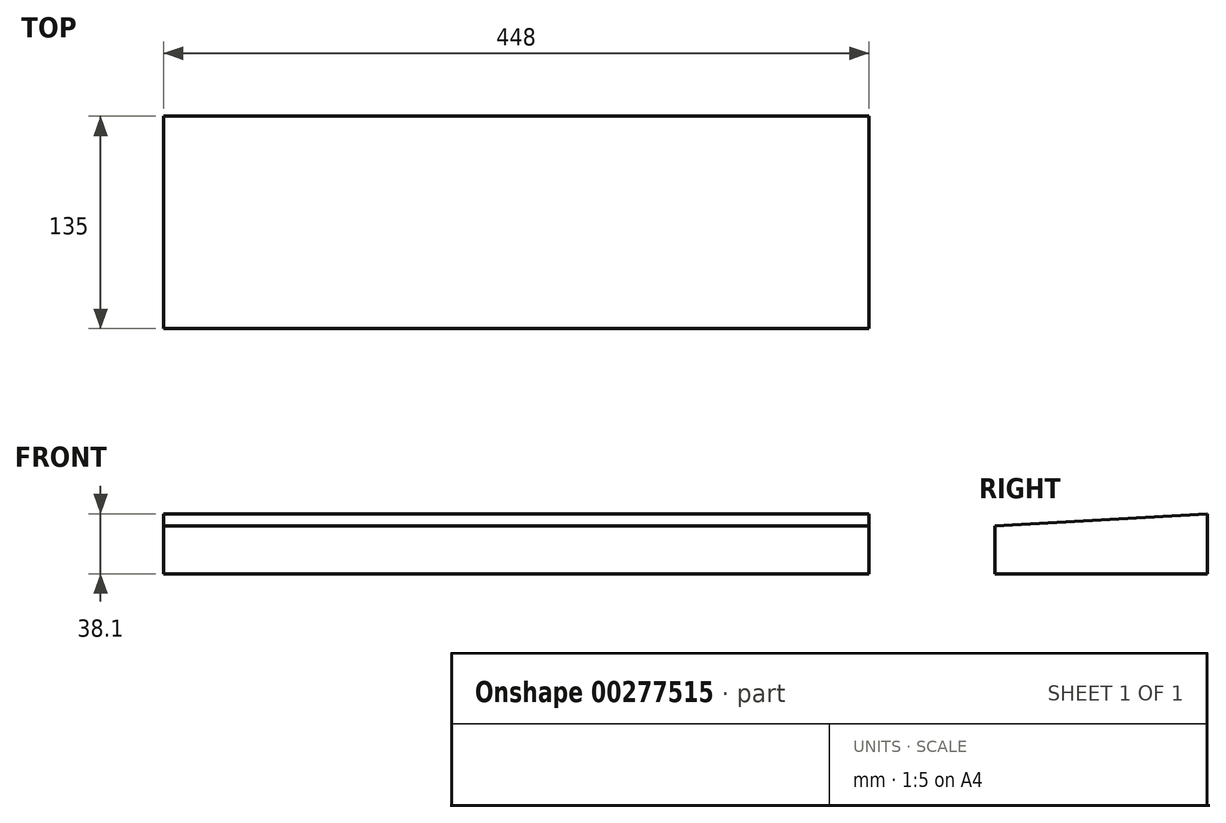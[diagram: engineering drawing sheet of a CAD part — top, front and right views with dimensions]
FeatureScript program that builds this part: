
annotation { "Feature Type Name" : "Feature", "Feature Type Description" : "" }
export const myFeature = defineFeature(function(context is Context, id is Id, definition is map)
    precondition{}
    {
        {
            var Q0;
            Q0=qCreatedBy(makeId("Right.planeOp"),FACE);
            var sketch = newSketch(context, id + "F0", { "sketchPlane" : qUnion([Q0])});
            skLineSegment(sketch, "E0.bottom", {"start": v(-67.5, 15.24) * mm, "end": v(67.5, 15.24) * mm});
            skLineSegment(sketch, "E0.top", {"start": v(-67.5, -15.24) * mm, "end": v(67.5, -15.24) * mm});
            skLineSegment(sketch, "E0.left", {"start": v(-67.5, 15.24) * mm, "end": v(-67.5, -15.24) * mm});
            skLineSegment(sketch, "E0.right", {"start": v(67.5, 15.24) * mm, "end": v(67.5, -15.24) * mm});
            skPoint(sketch, "E0.middle", {"position": v(0, 0) * mm});
            skLineSegment(sketch, "E1", {"start": v(-67.5, 15.24) * mm, "end": v(67.46, 22.86) * mm});
            skLineSegment(sketch, "E2", {"start": v(67.46, 22.86) * mm, "end": v(67.5, 15.24) * mm});
            skSolve(sketch);
        }
        {
            var Q0;
            Q0=makeQuery(id+"F0.imprint","IMPRINT",FACE,{"disambiguationData":[TD([[makeQuery(id+"F0.imprint","IMPRINT",EDGE,{"derivedFrom":sQuery(id+"F0.wireOp",EDGE,"E0.bottom")}),-1.0]])]});
            var Q1;
            Q1=makeQuery(id+"F0.imprint","IMPRINT",FACE,{"disambiguationData":[TD([[makeQuery(id+"F0.imprint","IMPRINT",EDGE,{"derivedFrom":sQuery(id+"F0.wireOp",EDGE,"E0.bottom")}),1.0]])]});
            extrude(context, id + "F1", {"entities" : qUnion([Q0, Q1]), "depth" : 448 * mm});
        }
    });
